# Revit family: Quad TBar
name_source: partatom
category: Lighting Fixtures
revit_build: Autodesk Revit 2018 (Build: 20190510_1515(x64)
units: mm (PartAtom-declared; Revit-internal decimal feet)

## family parameters
Always vertical = Yes
Cut with Voids When Loaded = No
Host = Ceiling
Light Source = Yes
Part Type = Normal
Room Calculation Point = No
Round Connector Dimension = Use Diameter
Shared = No

## types (5) — shared parameters
A Height = 3 "
Apparent Load = 0 VA
Bolt = White Painted Aluminum
Color Filter = 16777215
Depth = 8.25 "
Dimming Lamp Color Temperature Shift = <None>
Emit Shape Visible in Rendering = No
Emit from Circle Diameter = 24 "
Glass = Glass
Height = 3 "
Light A = Yes
Manufacturer = ARON
Material = White Painted Aluminum
Photometric Web File = edge-suspended-b4.ies
Poles = 1
Specification = https://www.aronlighting.com
Tilt Angle = 60.00°
URL = https://www.aronlighting.com
Voltage = 120 V
Width = 8.25 "

## per-type parameters (varying)
| type | B Height | C Height | D Height | Light B | Light C | Light D |
| QuadT1-FSQ-AR-BR-CR-DR | 3 " | 3 " | 3 " | Yes | Yes | Yes |
| QuadT1-FSQ-AR-BR-CX-DR | 3 " | 3 " | 0.04 " | Yes | Yes | No |
| QuadT1-FSQ-AR-BX-CR-DX | 0.04 " | 0.04 " | 3 " | No | No | Yes |
| QuadT1-FSQ-AR-BX-CX-DR | 0.04 " | 3 " | 0.04 " | No | Yes | No |
| QuadT1-FSQ-AR-BX-CX-DX | 0.04 " | 0.04 " | 0.04 " | No | No | No |

note: column(s) folded — value = type name in every type: Model

## geometry (parser evidence)
native form markers: Sweep x3
no freeform markers — native parametric forms only
